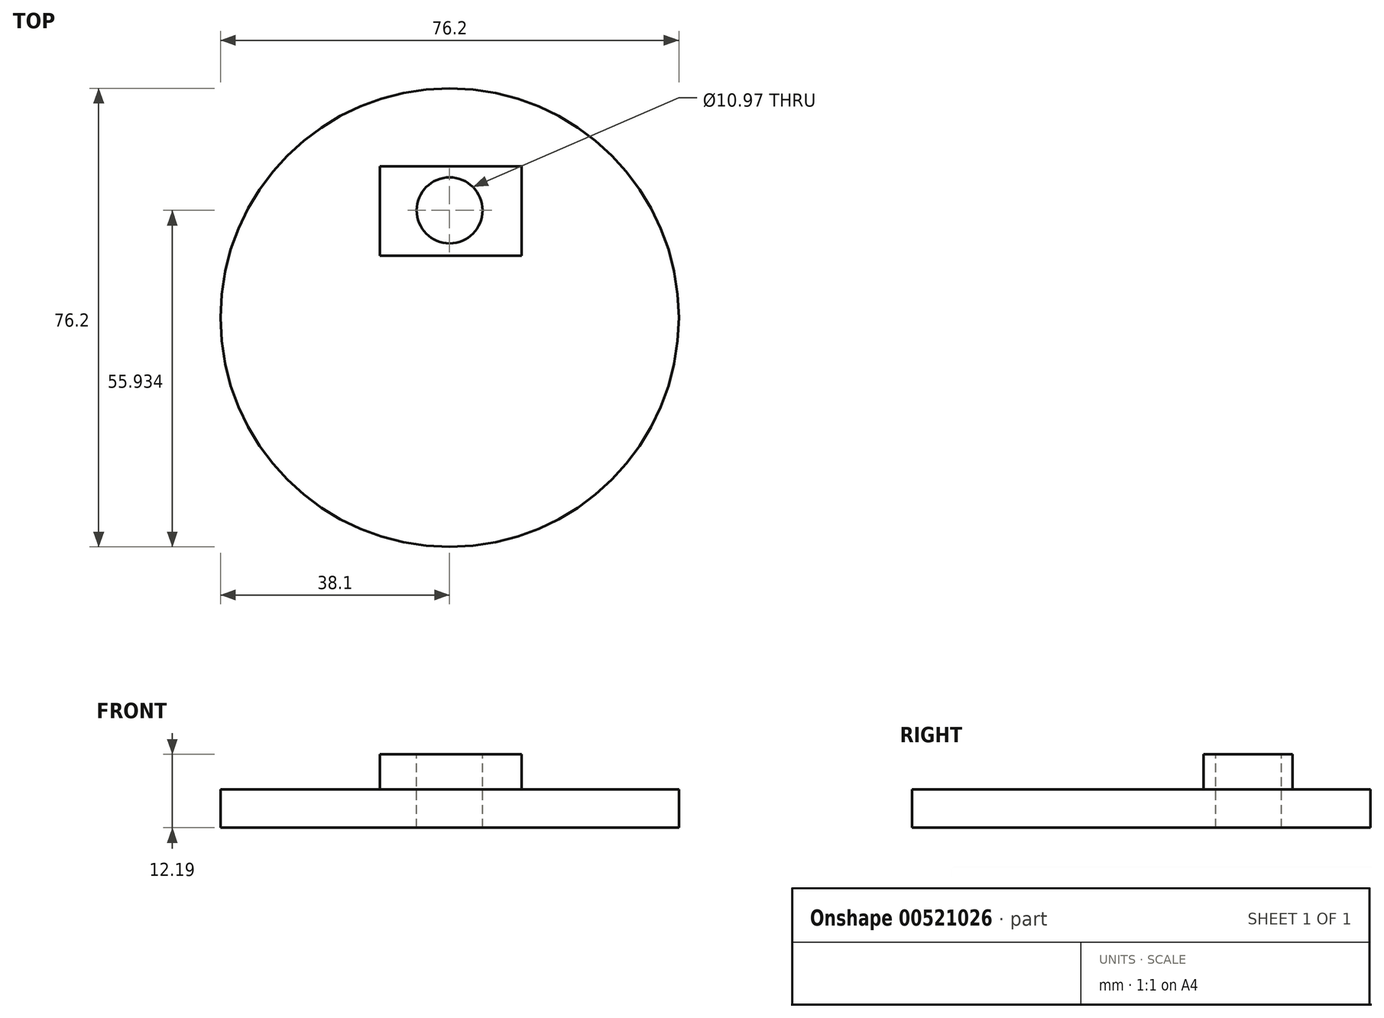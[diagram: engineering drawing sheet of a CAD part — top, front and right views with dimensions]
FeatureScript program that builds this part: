
annotation { "Feature Type Name" : "Feature", "Feature Type Description" : "" }
export const myFeature = defineFeature(function(context is Context, id is Id, definition is map)
    precondition{}
    {
        {
            var Q0;
            Q0=qCreatedBy(makeId("Top.planeOp"),FACE);
            var sketch = newSketch(context, id + "F0", { "sketchPlane" : qUnion([Q0])});
            skCircle(sketch, "E0", {"center": v(0, 0) * mm, "radius": 38.1 * mm});
            skSolve(sketch);
        }
        {
            var Q0;
            Q0 = qSketchRegion(id + "F0", true);
            extrude(context, id + "F1", {"entities" : qUnion([Q0]), "depth" : 6.35 * mm, "offsetDistance" : 25.4 * mm});
        }
        {
            var Q0;
            Q0=makeQuery(id+"F1.opExtrude","CAP_FACE",FACE,{"disambiguationData":[OSD([sQuery(id+"F0.wireOp",EDGE,"E0")])],"isStart":false});
            var sketch = newSketch(context, id + "F2", { "sketchPlane" : qUnion([Q0])});
            skLineSegment(sketch, "E1.bottom", {"start": v(-11.57, 25.16) * mm, "end": v(11.95, 25.16) * mm});
            skLineSegment(sketch, "E1.top", {"start": v(-11.57, 10.31) * mm, "end": v(11.95, 10.31) * mm});
            skLineSegment(sketch, "E1.left", {"start": v(-11.57, 25.16) * mm, "end": v(-11.57, 10.31) * mm});
            skLineSegment(sketch, "E1.right", {"start": v(11.95, 25.16) * mm, "end": v(11.95, 10.31) * mm});
            skSolve(sketch);
        }
        {
            var Q0;
            Q0 = qSketchRegion(id + "F2", true);
            extrude(context, id + "F3", {"entities" : qUnion([Q0]), "operationType" : NewBodyOperationType.ADD, "depth" : 5.84 * mm, "offsetDistance" : 25.4 * mm});
        }
        {
            var Q0;
            Q0=makeQuery(id+"F3.opExtrude","CAP_FACE",FACE,{"disambiguationData":[OSD([sQuery(id+"F2.wireOp",EDGE,"E1.bottom"),sQuery(id+"F2.wireOp",EDGE,"E1.top"),sQuery(id+"F2.wireOp",EDGE,"E1.left"),sQuery(id+"F2.wireOp",EDGE,"E1.right")])],"isStart":false});
            var sketch = newSketch(context, id + "F4", { "sketchPlane" : qUnion([Q0])});
            skCircle(sketch, "E2", {"center": v(0, 17.83) * mm, "radius": 5.48 * mm});
            skSolve(sketch);
        }
        {
            var Q0;
            Q0=makeQuery(id+"F4.imprint","IMPRINT",FACE,{"disambiguationData":[TD([[makeQuery(id+"F4.imprint","IMPRINT",EDGE,{"derivedFrom":sQuery(id+"F4.wireOp",EDGE,"E2")}),1.0]])]});
            var Q1;
            Q1=sQuery(id+"F4.wireOp",EDGE,"E2");
            extrude(context, id + "F5", {"entities" : qUnion([Q0]), "operationType" : NewBodyOperationType.REMOVE, "surfaceEntities" : qUnion([Q1]), "oppositeDirection" : true, "depth" : 27.94 * mm, "offsetDistance" : 25.4 * mm});
        }
    });
